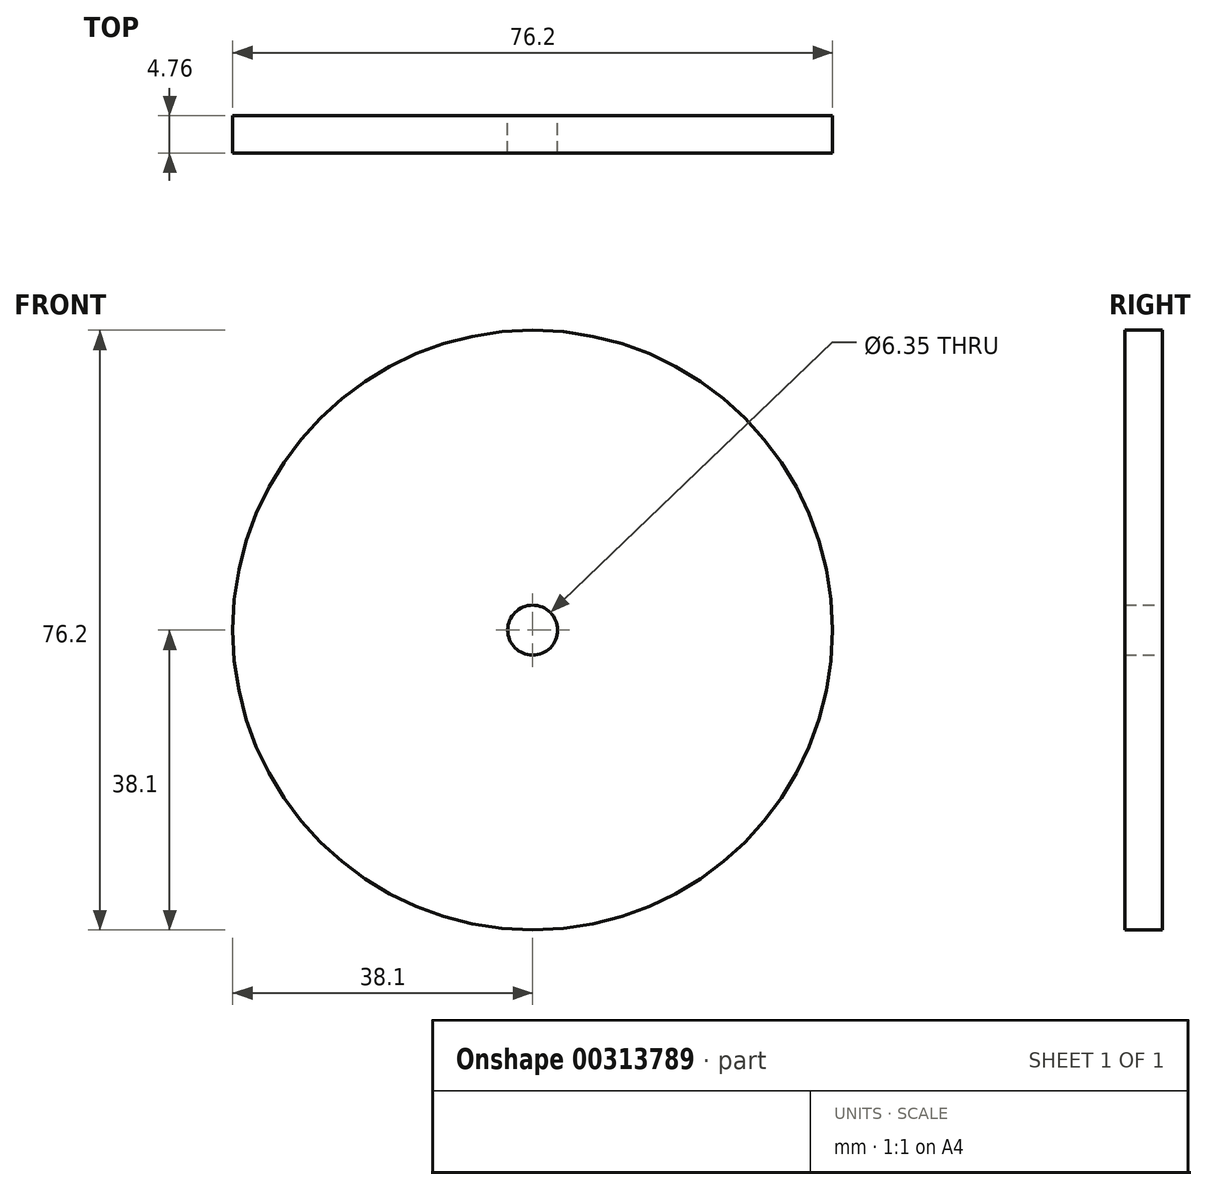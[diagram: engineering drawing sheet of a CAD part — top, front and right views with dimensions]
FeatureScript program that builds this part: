
annotation { "Feature Type Name" : "Feature", "Feature Type Description" : "" }
export const myFeature = defineFeature(function(context is Context, id is Id, definition is map)
    precondition{}
    {
        {
            var Q0;
            Q0=qCreatedBy(makeId("Front.planeOp"),FACE);
            var sketch = newSketch(context, id + "F0", { "sketchPlane" : qUnion([Q0])});
            skCircle(sketch, "E0", {"center": v(0, 0) * mm, "radius": 38.1 * mm});
            skCircle(sketch, "E1", {"center": v(0, 0) * mm, "radius": 3.18 * mm});
            skSolve(sketch);
        }
        {
            var Q0;
            Q0=makeQuery(id+"F0.imprint","IMPRINT",FACE,{"disambiguationData":[TD([[makeQuery(id+"F0.imprint","IMPRINT",EDGE,{"derivedFrom":sQuery(id+"F0.wireOp",EDGE,"E0")}),1.0]])]});
            extrude(context, id + "F1", {"entities" : qUnion([Q0]), "endBound" : BoundingType.SYMMETRIC, "depth" : 4.76 * mm});
        }
    });
